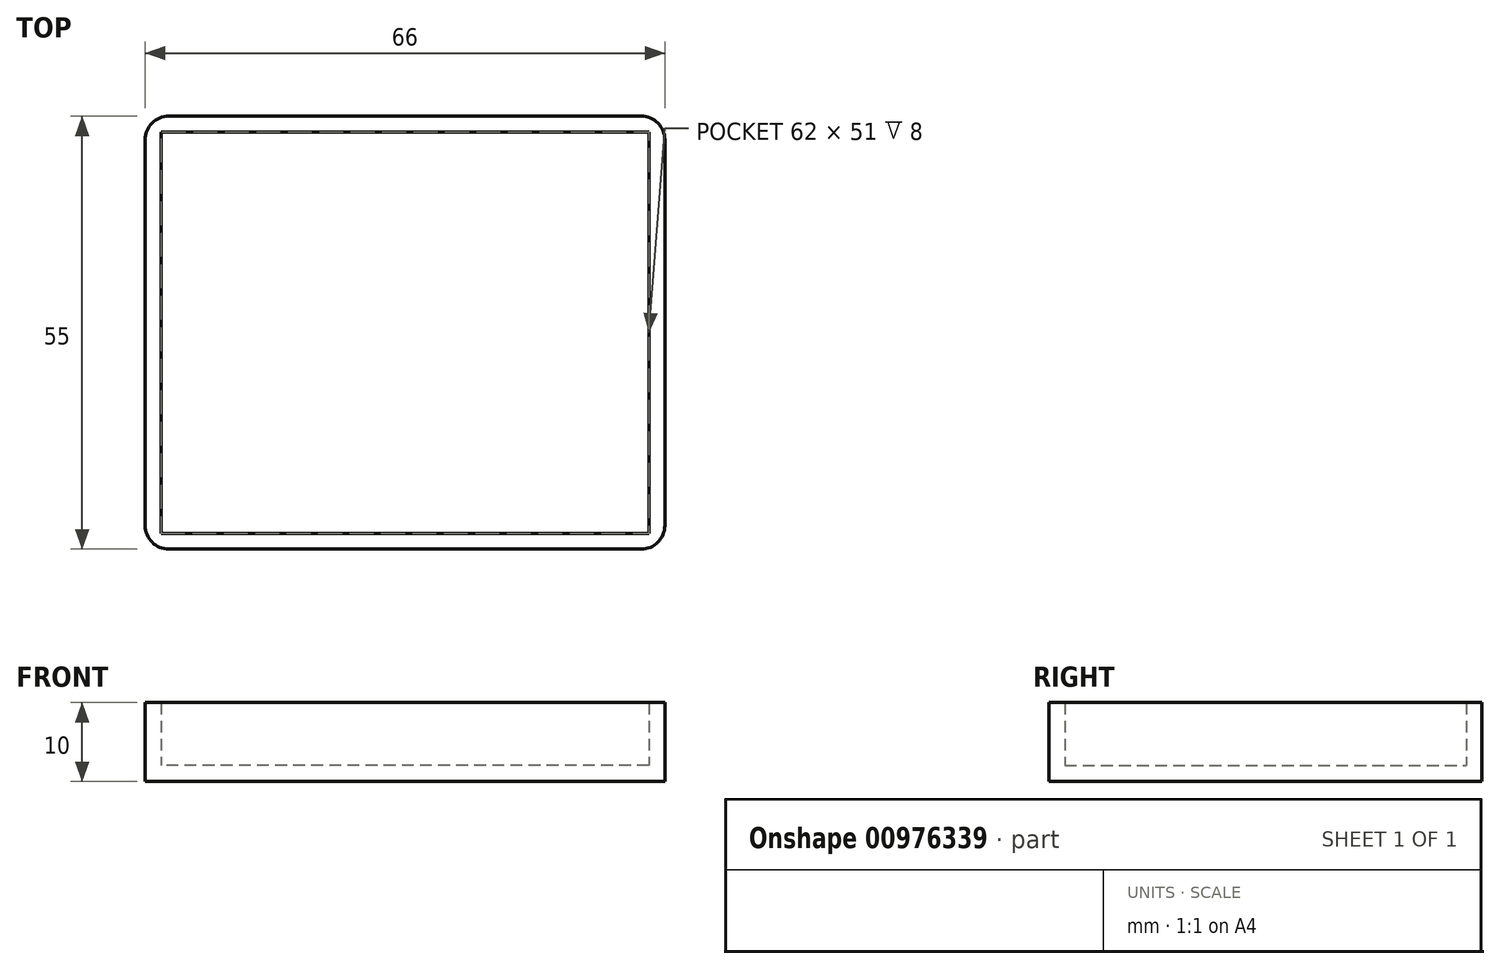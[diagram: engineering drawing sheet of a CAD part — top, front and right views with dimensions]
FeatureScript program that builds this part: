
annotation { "Feature Type Name" : "Feature", "Feature Type Description" : "" }
export const myFeature = defineFeature(function(context is Context, id is Id, definition is map)
    precondition{}
    {
        {
            var Q0;
            Q0=qCreatedBy(makeId("Top.planeOp"),FACE);
            var sketch = newSketch(context, id + "F0", { "sketchPlane" : qUnion([Q0])});
            skLineSegment(sketch, "E0.bottom", {"start": v(0, 0) * mm, "end": v(-66, 0) * mm});
            skLineSegment(sketch, "E0.top", {"start": v(0, 55) * mm, "end": v(-66, 55) * mm});
            skLineSegment(sketch, "E0.left", {"start": v(0, 0) * mm, "end": v(0, 55) * mm});
            skLineSegment(sketch, "E0.right", {"start": v(-66, 0) * mm, "end": v(-66, 55) * mm});
            skSolve(sketch);
        }
        {
            var Q0;
            Q0=makeQuery(id+"F0.imprint","IMPRINT",FACE,{"disambiguationData":[TD([[makeQuery(id+"F0.imprint","IMPRINT",EDGE,{"derivedFrom":sQuery(id+"F0.wireOp",EDGE,"E0.bottom")}),-1.0]])]});
            extrude(context, id + "F1", {"entities" : qUnion([Q0]), "depth" : 10 * mm, "offsetDistance" : 25 * mm});
        }
        {
            var Q0;
            Q0=makeQuery(id+"F1.opExtrude","CAP_FACE",FACE,{"disambiguationData":[OSD([sQuery(id+"F0.wireOp",EDGE,"E0.bottom"),sQuery(id+"F0.wireOp",EDGE,"E0.top"),sQuery(id+"F0.wireOp",EDGE,"E0.left"),sQuery(id+"F0.wireOp",EDGE,"E0.right")])],"isStart":false});
            shell(context, id + "F2", {"entities" : qUnion([Q0]), "thickness" : 2 * mm});
        }
        {
            var Q0;
            Q0=makeQuery(id+"F1.opExtrude","SWEPT_EDGE",EDGE,{"disambiguationData":[OSD([sQuery(id+"F0.wireOp",EDGE,"E0.top"),sQuery(id+"F0.wireOp",EDGE,"E0.left")])]});
            fillet(context, id + "F3", {"entities" : qUnion([Q0]), "radius" : 3 * mm, "tangentPropagation" : true, "allowEdgeOverflow" : false});
        }
        {
            var Q0;
            Q0=makeQuery(id+"F1.opExtrude","SWEPT_EDGE",EDGE,{"disambiguationData":[OSD([sQuery(id+"F0.wireOp",EDGE,"E0.bottom"),sQuery(id+"F0.wireOp",EDGE,"E0.left")])]});
            fillet(context, id + "F4", {"entities" : qUnion([Q0]), "radius" : 3 * mm, "tangentPropagation" : true, "allowEdgeOverflow" : false});
        }
        {
            var Q0;
            Q0=makeQuery(id+"F1.opExtrude","SWEPT_EDGE",EDGE,{"disambiguationData":[OSD([sQuery(id+"F0.wireOp",EDGE,"E0.top"),sQuery(id+"F0.wireOp",EDGE,"E0.right")])]});
            fillet(context, id + "F5", {"entities" : qUnion([Q0]), "radius" : 3 * mm, "tangentPropagation" : true, "allowEdgeOverflow" : false});
        }
        {
            var Q0;
            Q0=makeQuery(id+"F1.opExtrude","SWEPT_EDGE",EDGE,{"disambiguationData":[OSD([sQuery(id+"F0.wireOp",EDGE,"E0.bottom"),sQuery(id+"F0.wireOp",EDGE,"E0.right")])]});
            fillet(context, id + "F6", {"entities" : qUnion([Q0]), "radius" : 3 * mm, "tangentPropagation" : true, "allowEdgeOverflow" : false});
        }
    });
